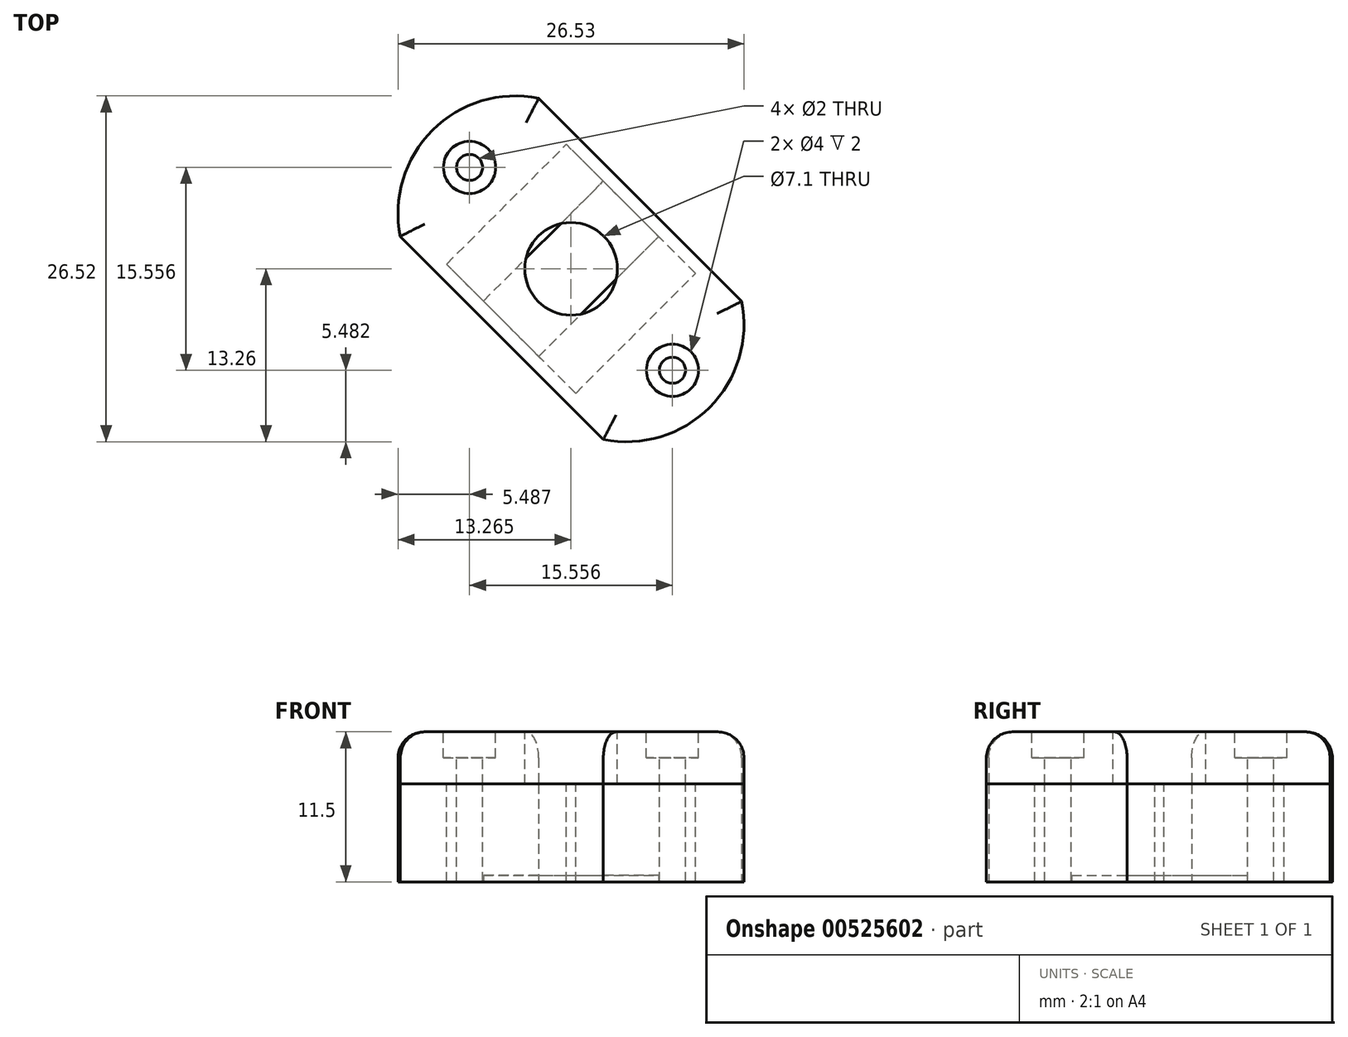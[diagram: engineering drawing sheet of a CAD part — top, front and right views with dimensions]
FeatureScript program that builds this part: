
annotation { "Feature Type Name" : "Feature", "Feature Type Description" : "" }
export const myFeature = defineFeature(function(context is Context, id is Id, definition is map)
    precondition{}
    {
        {
            var Q0;
            Q0=qCreatedBy(makeId("Top.planeOp"),FACE);
            var sketch = newSketch(context, id + "F0", { "sketchPlane" : qUnion([Q0])});
            skLineSegment(sketch, "E0.top", {"start": v(-34, -36.04) * mm, "end": v(-56, -36.04) * mm});
            skLineSegment(sketch, "E0.left", {"start": v(-34, -51.04) * mm, "end": v(-34, -36.04) * mm});
            skLineSegment(sketch, "E0.right", {"start": v(-56, -51.04) * mm, "end": v(-56, -36.04) * mm});
            skPoint(sketch, "E0.middle", {"position": v(-45, -43.54) * mm});
            skArc(sketch, "E1", {"start": v(-34, -51.04) * mm, "mid": v(-29.97, -43.54) * mm, "end": v(-34, -36.04) * mm});
            skArc(sketch, "E2", {"start": v(-56, -36.04) * mm, "mid": v(-60.03, -43.54) * mm, "end": v(-56, -51.04) * mm});
            skLineSegment(sketch, "E3", {"start": v(-56, -51.04) * mm, "end": v(-34, -51.04) * mm});
            skSolve(sketch);
        }
        {
            var Q0;
            Q0=qSketchRegion(id+"F0",true);
            extrude(context, id + "F1", {"entities" : qUnion([Q0]), "depth" : 7.5 * mm, "offsetDistance" : 25 * mm});
        }
        {
            var Q0;
            Q0=makeQuery(id+"F1.opExtrude","CAP_FACE",FACE,{"disambiguationData":[OSD([sQuery(id+"F0.wireOp",EDGE,"E0.bottom"),sQuery(id+"F0.wireOp",EDGE,"E0.top"),sQuery(id+"F0.wireOp",EDGE,"E0.left"),sQuery(id+"F0.wireOp",EDGE,"E0.right")])],"isStart":false});
            var sketch = newSketch(context, id + "F2", { "sketchPlane" : qUnion([Q0])});
            skCircle(sketch, "E4", {"center": v(-56, -43.54) * mm, "radius": 1 * mm});
            skCircle(sketch, "E5", {"center": v(-34, -43.54) * mm, "radius": 1 * mm});
            skCircle(sketch, "E6", {"center": v(-45, -43.54) * mm, "radius": 3.55 * mm, "construction": true});
            skLineSegment(sketch, "E7.bottom", {"start": v(-38, -50.04) * mm, "end": v(-52, -50.04) * mm});
            skLineSegment(sketch, "E7.top", {"start": v(-38, -37.04) * mm, "end": v(-52, -37.04) * mm});
            skLineSegment(sketch, "E7.left", {"start": v(-38, -50.04) * mm, "end": v(-38, -37.04) * mm});
            skLineSegment(sketch, "E7.right", {"start": v(-52, -50.04) * mm, "end": v(-52, -37.04) * mm});
            skSolve(sketch);
        }
        {
            var Q0;
            Q0=qSketchRegion(id+"F2",true);
            extrude(context, id + "F3", {"entities" : qUnion([Q0]), "operationType" : NewBodyOperationType.REMOVE, "oppositeDirection" : true, "depth" : 7.5 * mm, "offsetDistance" : 25 * mm});
        }
        {
            var Q0;
            Q0=makeQuery(id+"F1.opExtrude","CAP_FACE",FACE,{"disambiguationData":[OSD([sQuery(id+"F0.wireOp",EDGE,"E0.top"),sQuery(id+"F0.wireOp",EDGE,"E1"),sQuery(id+"F0.wireOp",EDGE,"E2"),sQuery(id+"F0.wireOp",EDGE,"E3")])],"isStart":true});
            var sketch = newSketch(context, id + "F4", { "sketchPlane" : qUnion([Q0])});
            skPoint(sketch, "E8.middle.positionSnap0", {"position": v(-45, 37.04) * mm});
            skPoint(sketch, "E8.centerSnap0", {"position": v(-45, 37.04) * mm});
            skLineSegment(sketch, "E9.bottom", {"start": v(-42, 50.04) * mm, "end": v(-48, 50.04) * mm});
            skLineSegment(sketch, "E9.top", {"start": v(-42, 37.04) * mm, "end": v(-48, 37.04) * mm});
            skLineSegment(sketch, "E9.left", {"start": v(-42, 50.04) * mm, "end": v(-42, 37.04) * mm});
            skLineSegment(sketch, "E9.right", {"start": v(-48, 50.04) * mm, "end": v(-48, 37.04) * mm});
            skPoint(sketch, "E9.middle", {"position": v(-45, 43.54) * mm});
            skPoint(sketch, "E9.middle.positionSnap0", {"position": v(-38, 43.54) * mm});
            skPoint(sketch, "E9.centerSnap0", {"position": v(-38, 43.54) * mm});
            skSolve(sketch);
        }
        {
            var Q0;
            Q0=qSketchRegion(id+"F4",true);
            extrude(context, id + "F5", {"entities" : qUnion([Q0]), "operationType" : NewBodyOperationType.ADD, "oppositeDirection" : true, "depth" : 0.5 * mm, "offsetDistance" : 25 * mm});
        }
        {
            var Q0;
            Q0=makeQuery(id+"F1.opExtrude","CAP_FACE",FACE,{"disambiguationData":[OSD([sQuery(id+"F0.wireOp",EDGE,"E0.top"),sQuery(id+"F0.wireOp",EDGE,"E1"),sQuery(id+"F0.wireOp",EDGE,"E2"),sQuery(id+"F0.wireOp",EDGE,"E3")])],"isStart":false});
            var sketch = newSketch(context, id + "F6", { "sketchPlane" : qUnion([Q0])});
            skLineSegment(sketch, "E10.top", {"start": v(-34, -36.04) * mm, "end": v(-56, -36.04) * mm});
            skLineSegment(sketch, "E10.left", {"start": v(-34, -51.04) * mm, "end": v(-34, -36.04) * mm});
            skLineSegment(sketch, "E10.right", {"start": v(-56, -51.04) * mm, "end": v(-56, -36.04) * mm});
            skPoint(sketch, "E10.middle", {"position": v(-45, -43.54) * mm});
            skArc(sketch, "E11", {"start": v(-34, -51.04) * mm, "mid": v(-29.97, -43.54) * mm, "end": v(-34, -36.04) * mm});
            skArc(sketch, "E12", {"start": v(-56, -36.04) * mm, "mid": v(-60.03, -43.54) * mm, "end": v(-56, -51.04) * mm});
            skLineSegment(sketch, "E13", {"start": v(-56, -51.04) * mm, "end": v(-34, -51.04) * mm});
            skPoint(sketch, "E14", {"position": v(-38, -43.54) * mm});
            skPoint(sketch, "E15", {"position": v(-45, -37.04) * mm});
            skSolve(sketch);
        }
        {
            var Q0;
            Q0=qSketchRegion(id+"F6",true);
            extrude(context, id + "F7", {"entities" : qUnion([Q0]), "depth" : 4 * mm, "offsetDistance" : 25 * mm});
        }
        {
            var Q0;
            Q0=makeQuery(id+"F7.opExtrude","CAP_FACE",FACE,{"disambiguationData":[OSD([sQuery(id+"F6.wireOp",EDGE,"E10.top"),sQuery(id+"F6.wireOp",EDGE,"E11"),sQuery(id+"F6.wireOp",EDGE,"E12"),sQuery(id+"F6.wireOp",EDGE,"E13")])],"isStart":false});
            var sketch = newSketch(context, id + "F8", { "sketchPlane" : qUnion([Q0])});
            skCircle(sketch, "E16", {"center": v(-56, -43.54) * mm, "radius": 1 * mm, "construction": true});
            skCircle(sketch, "E17", {"center": v(-34, -43.54) * mm, "radius": 1 * mm, "construction": true});
            skCircle(sketch, "E18", {"center": v(-45, -43.54) * mm, "radius": 3.55 * mm});
            skPoint(sketch, "E19", {"position": v(-29.97, -43.54) * mm});
            skPoint(sketch, "E20", {"position": v(-45, -51.04) * mm});
            skSolve(sketch);
        }
        {
            var Q0;
            Q0=qSketchRegion(id+"F8",true);
            extrude(context, id + "F9", {"entities" : qUnion([Q0]), "operationType" : NewBodyOperationType.REMOVE, "oppositeDirection" : true, "depth" : 4 * mm, "offsetDistance" : 25 * mm});
        }
        {
            var Q0;
            Q0=makeQuery(id+"F7.opExtrude","CAP_EDGE",EDGE,{"disambiguationData":[OSD([sQuery(id+"F6.wireOp",EDGE,"E11")])],"isStart":false});
            var Q1;
            Q1=makeQuery(id+"F7.opExtrude","CAP_EDGE",EDGE,{"disambiguationData":[OSD([sQuery(id+"F6.wireOp",EDGE,"E10.top")])],"isStart":false});
            var Q2;
            Q2=makeQuery(id+"F7.opExtrude","CAP_EDGE",EDGE,{"disambiguationData":[OSD([sQuery(id+"F6.wireOp",EDGE,"E12")])],"isStart":false});
            var Q3;
            Q3=makeQuery(id+"F7.opExtrude","CAP_EDGE",EDGE,{"disambiguationData":[OSD([sQuery(id+"F6.wireOp",EDGE,"E13")])],"isStart":false});
            fillet(context, id + "F10", {"entities" : qUnion([Q0, Q1, Q2, Q3]), "radius" : 2 * mm, "tangentPropagation" : true, "allowEdgeOverflow" : false});
        }
        {
            var Q0;
            Q0=sQuery(id+"F8.wireOp",VERTEX,"E17.center");
            var Q1;
            Q1=sQuery(id+"F8.wireOp",VERTEX,"E16.center");
            var Q2;
            Q2=makeQuery(id+"F7.opExtrude","SWEPT_BODY",BODY,{"disambiguationData":[OSD([sQuery(id+"F6.wireOp",EDGE,"E10.top"),sQuery(id+"F6.wireOp",EDGE,"E11"),sQuery(id+"F6.wireOp",EDGE,"E12"),sQuery(id+"F6.wireOp",EDGE,"E13")])]});
            hole(context, id + "F11", {"style" : HoleStyle.C_BORE, "endStyle" : HoleEndStyle.BLIND, "holeDiameter" : 2 * mm, "cBoreDiameter" : 4 * mm, "cBoreDepth" : 2 * mm, "majorDiameter" : 5 * mm, "holeDepth" : 20 * mm, "tappedDepth" : 12 * mm, "tapClearance" : 3, "locations" : qUnion([Q0, Q1]), "scope" : qUnion([Q2])});
        }
        {
            var Q0;
            Q0=makeQuery(id+"F1.opExtrude","SWEPT_BODY",BODY,{"disambiguationData":[OSD([sQuery(id+"F0.wireOp",EDGE,"E0.top"),sQuery(id+"F0.wireOp",EDGE,"E1"),sQuery(id+"F0.wireOp",EDGE,"E2"),sQuery(id+"F0.wireOp",EDGE,"E3")])]});
            var Q1;
            Q1=makeQuery(id+"F7.opExtrude","SWEPT_BODY",BODY,{"disambiguationData":[OSD([sQuery(id+"F6.wireOp",EDGE,"E10.top"),sQuery(id+"F6.wireOp",EDGE,"E11"),sQuery(id+"F6.wireOp",EDGE,"E12"),sQuery(id+"F6.wireOp",EDGE,"E13")])]});
            var Q2;
            Q2=makeQuery(id+"F1.opExtrude","SWEPT_EDGE",EDGE,{"disambiguationData":[OSD([sQuery(id+"F0.wireOp",EDGE,"E0.left"),sQuery(id+"F0.wireOp",EDGE,"E1"),sQuery(id+"F0.wireOp",EDGE,"E3")])]});
            transform(context, id + "F12", {"entities" : qUnion([Q0, Q1]), "transformType" : TransformType.ROTATION, "transformAxis" : qUnion([Q2]), "angle" : 45 * degree, "makeCopy" : false});
        }
    });
